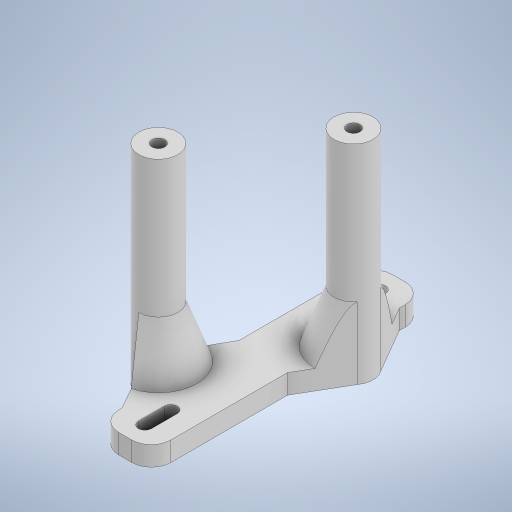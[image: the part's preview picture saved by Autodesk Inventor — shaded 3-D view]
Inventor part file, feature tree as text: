
AUTODESK INVENTOR PART (.ipt)
format: ipt  version: 2023.2 (Build 272271030, 271C)  size: 354,304 bytes
history: native  units: mm
features: chamfer x6, extrude x4, sketch x2
ambient origin geometry x8: Origin, YZ Plane, XZ Plane, XY Plane, X Axis, Y Axis, Z Axis, Center Point
bodies: Solid1 (feature_tree)
feature tree (12):
  sketch  "Sketch1"  dims[d4=2.0mm d7=2.0mm]
  extrude  "Extrusion2"  Depth=2.0mm
  extrude  "Extrusion3"  Depth=8.0mm
  extrude  "Extrusion4"  Depth=8.0mm
  chamfer  "Chamfer1"  Distance=2.0mm
  chamfer  "Chamfer2"  Distance=16.0mm
  chamfer  "Chamfer3"  Distance=42.0mm
  chamfer  "Chamfer4"  Distance=8.0mm
  chamfer  "Chamfer5"  Distance=3.0mm
  chamfer  "Chamfer6"  Distance=19.9mm
  extrude  "Extrusion5"  Depth=8.0mm
  sketch  "Sketch2"  dims[d14=2.0mm d15=16.0mm d16=2.0mm d17=2.0mm d18=16.0mm d19=42.0mm d21=8.0mm d22=3.0mm d24=19.9mm d31=2.54mm d33=17.0mm d34=19.9mm d36=15.5mm d37=5.0mm d38=4.0mm d39=2.0mm d40=1.5mm d43=32.0mm d44=0.0mm d45=4.0mm d46=6.0mm d47=32.0mm d48=0.0mm d49=3.0mm d50=0.0mm d51=7.55mm d52=4.0mm d53=6.0mm d54=60.0deg d55=4.0mm d56=6.0mm d57=60.0deg d58=6.0mm d59=3.4mm d60=60.0deg d61=3.4mm d62=6.0mm d63=60.0deg d64=6.0mm d65=2.0mm d66=8.0mm d67=2.0mm d68=3.490659mm d69=8.0mm d70=2.0mm d71=3.490659mm d72=2.0mm d73=2.0mm d74=8.0mm d75=0.0mm]
